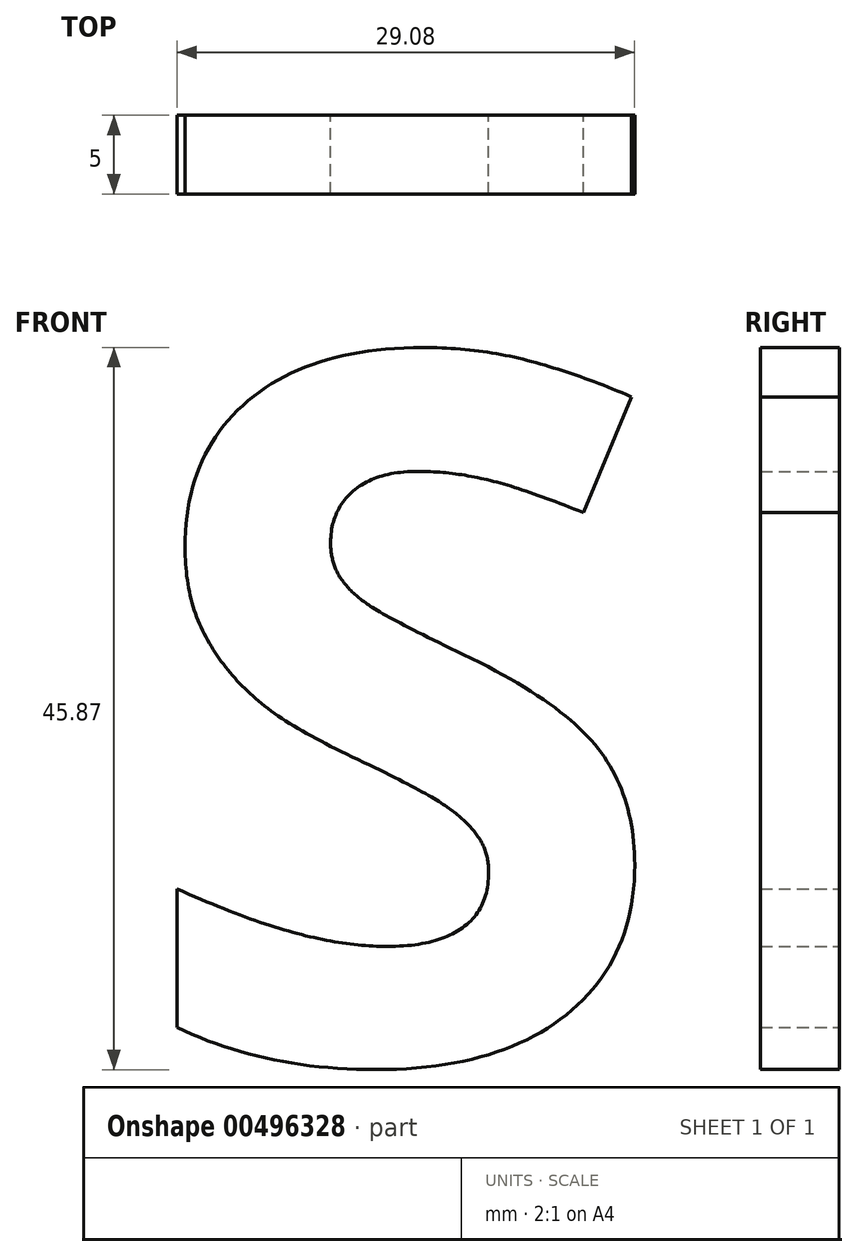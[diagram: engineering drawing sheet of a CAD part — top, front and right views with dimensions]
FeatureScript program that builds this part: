
annotation { "Feature Type Name" : "Feature", "Feature Type Description" : "" }
export const myFeature = defineFeature(function(context is Context, id is Id, definition is map)
    precondition{}
    {
        {
            var Q0;
            Q0=qCreatedBy(makeId("Front.planeOp"),FACE);
            var sketch = newSketch(context, id + "F0", { "sketchPlane" : qUnion([Q0])});
            skText(sketch, "E0", { "text": "S", "fontName": "OpenSans-Bold.ttf"});
            const initialGuessF0  = {"E0": [-0.05835, 0.01178, 1, 0, 0.045]};
            skSetInitialGuess(sketch, initialGuessF0);
            skSolve(sketch);
        }
        {
            var Q0;
            Q0=makeQuery(id+"F0.imprint","IMPRINT",FACE,{"disambiguationData":[TD([[makeQuery(id+"F0.imprint","IMPRINT",EDGE,{"derivedFrom":sQuery(id+"F0.wireOp",EDGE,"E0.sketch_text.stroke-0")}),-1.0]])]});
            extrude(context, id + "F1", {"entities" : qUnion([Q0]), "depth" : 5 * mm});
        }
    });
